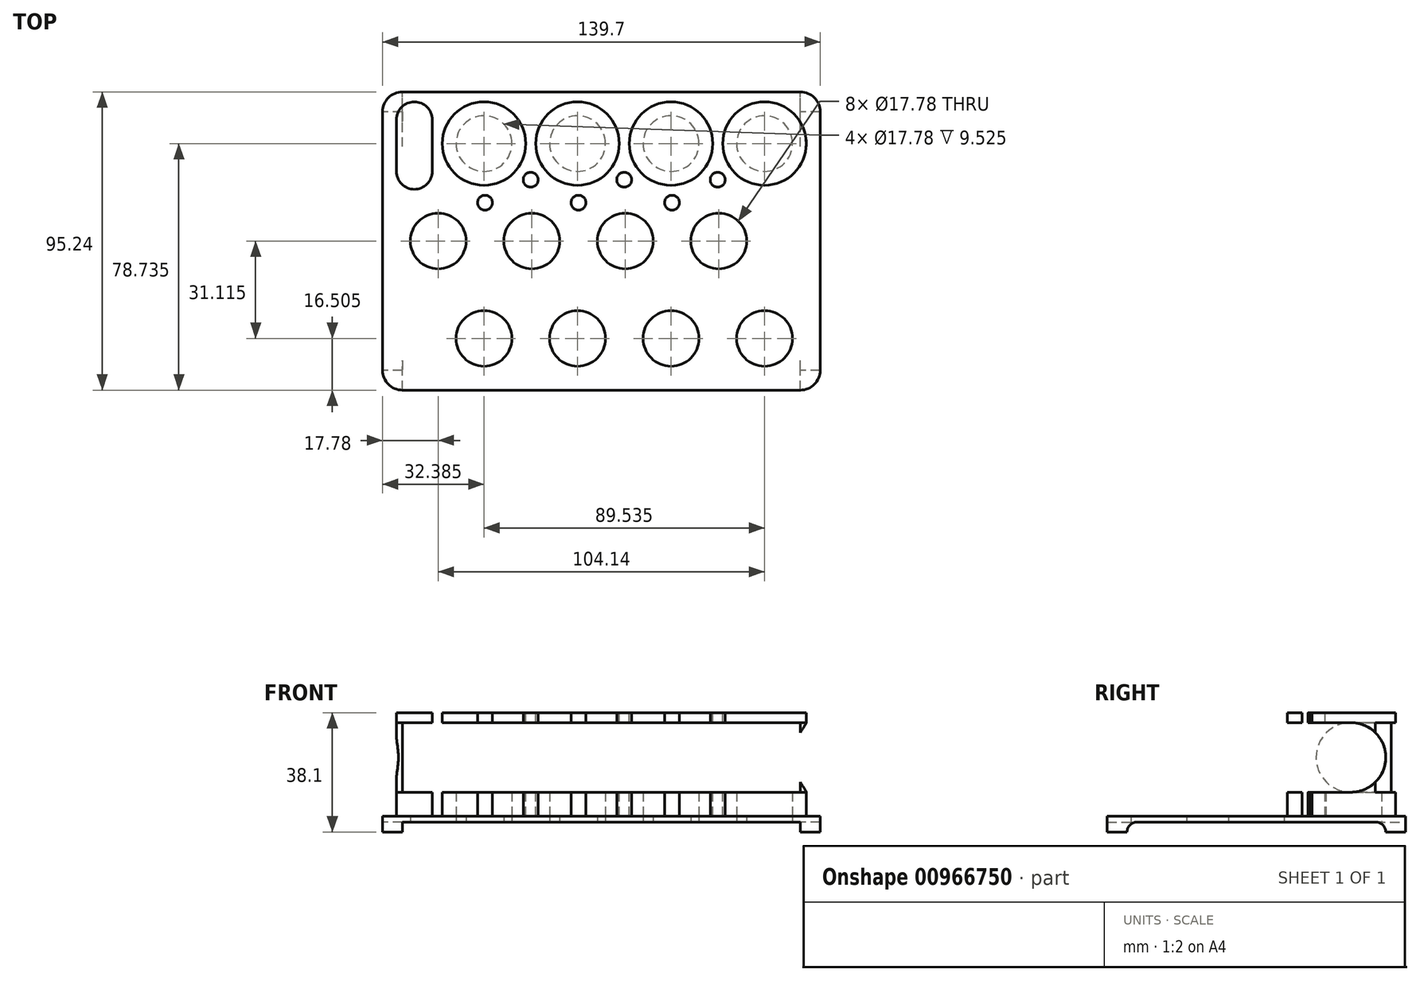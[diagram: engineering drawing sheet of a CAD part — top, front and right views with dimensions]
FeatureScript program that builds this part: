
annotation { "Feature Type Name" : "Feature", "Feature Type Description" : "" }
export const myFeature = defineFeature(function(context is Context, id is Id, definition is map)
    precondition{}
    {
        {
            var Q0;
            Q0=qCreatedBy(makeId("Right.planeOp"),FACE);
            var sketch = newSketch(context, id + "F0", { "sketchPlane" : qUnion([Q0])});
            skLineSegment(sketch, "E0.top", {"start": v(47.63, -19.05) * mm, "end": v(-47.63, -19.05) * mm});
            skLineSegment(sketch, "E0.left", {"start": v(47.63, 19.05) * mm, "end": v(47.63, -19.05) * mm});
            skLineSegment(sketch, "E0.right", {"start": v(-47.63, 19.05) * mm, "end": v(-47.63, -19.05) * mm});
            skPoint(sketch, "E0.middle", {"position": v(0, 0) * mm});
            skLineSegment(sketch, "E1.bottom", {"start": v(-41.28, -19.05) * mm, "end": v(41.27, -19.05) * mm});
            skLineSegment(sketch, "E1.top", {"start": v(-41.28, -15.88) * mm, "end": v(41.27, -15.88) * mm});
            skLineSegment(sketch, "E1.left", {"start": v(-41.28, -19.05) * mm, "end": v(-41.28, -19.05) * mm});
            skLineSegment(sketch, "E1.right", {"start": v(41.27, -19.05) * mm, "end": v(41.27, -19.05) * mm});
            skLineSegment(sketch, "E2.bottom", {"start": v(-30.16, -6.35) * mm, "end": v(30.16, -6.35) * mm});
            skLineSegment(sketch, "E2.top", {"start": v(-30.16, 15.88) * mm, "end": v(30.16, 15.88) * mm});
            skLineSegment(sketch, "E2.left", {"start": v(-41.28, 4.76) * mm, "end": v(-41.28, 4.76) * mm});
            skLineSegment(sketch, "E2.right", {"start": v(41.28, 4.76) * mm, "end": v(41.28, 4.76) * mm});
            skPoint(sketch, "E3.visualSharp", {"position": v(-41.28, -6.35) * mm});
            skPoint(sketch, "E4.visualSharp", {"position": v(41.28, -6.35) * mm});
            skPoint(sketch, "E5.visualSharp", {"position": v(-41.28, -15.88) * mm});
            skPoint(sketch, "E6.visualSharp", {"position": v(41.27, -15.88) * mm});
            skLineSegment(sketch, "E7", {"start": v(41.27, -15.88) * mm, "end": v(41.27, -15.88) * mm});
            skLineSegment(sketch, "E8", {"start": v(41.27, -15.88) * mm, "end": v(41.27, -19.05) * mm});
            skLineSegment(sketch, "E9", {"start": v(-41.28, -15.88) * mm, "end": v(-41.28, -15.88) * mm});
            skLineSegment(sketch, "E10", {"start": v(-41.28, -15.88) * mm, "end": v(-41.28, -19.05) * mm});
            skLineSegment(sketch, "E11", {"start": v(-41.28, -6.35) * mm, "end": v(-41.28, -6.35) * mm});
            skLineSegment(sketch, "E12", {"start": v(41.28, -6.35) * mm, "end": v(41.28, -6.35) * mm});
            skLineSegment(sketch, "E13", {"start": v(-47.63, 19.05) * mm, "end": v(47.63, 19.05) * mm});
            skArc(sketch, "E14.filletArc", {"start": v(-30.16, 15.88) * mm, "mid": v(-38.02, 12.62) * mm, "end": v(-41.28, 4.76) * mm});
            skArc(sketch, "E15.filletArc", {"start": v(-41.28, 4.76) * mm, "mid": v(-38.02, -3.1) * mm, "end": v(-30.16, -6.35) * mm});
            skArc(sketch, "E16.filletArc", {"start": v(41.28, 4.76) * mm, "mid": v(38.02, 12.62) * mm, "end": v(30.16, 15.88) * mm});
            skArc(sketch, "E17.filletArc", {"start": v(30.16, -6.35) * mm, "mid": v(38.02, -3.1) * mm, "end": v(41.28, 4.76) * mm});
            skSolve(sketch);
        }
        {
            var Q0;
            {var subQ0=sQuery(id+"F0.wireOp",EDGE,"E0.left");Q0=makeQuery(id+"F0.imprint","IMPRINT",FACE,{"disambiguationData":[TD([[makeQuery(id+"F0.imprint","IMPRINT",EDGE,{"derivedFrom":subQ0}),-1.0]])]});}
            extrude(context, id + "F1", {"entities" : qUnion([Q0]), "depth" : 139.7 * mm, "offsetDistance" : 25.4 * mm});
        }
        {
            var Q0;
            Q0=makeQuery(id+"F1.opExtrude","SWEPT_FACE",FACE,{"disambiguationData":[OSD([sQuery(id+"F0.wireOp",EDGE,"E0.left")])]});
            var sketch = newSketch(context, id + "F2", { "sketchPlane" : qUnion([Q0])});
            skLineSegment(sketch, "E18.bottom", {"start": v(-133.35, -19.05) * mm, "end": v(-6.35, -19.05) * mm});
            skLineSegment(sketch, "E18.top", {"start": v(-133.35, -15.88) * mm, "end": v(-6.35, -15.88) * mm});
            skLineSegment(sketch, "E18.left", {"start": v(-133.35, -19.05) * mm, "end": v(-133.35, -19.05) * mm});
            skLineSegment(sketch, "E18.right", {"start": v(-6.35, -19.05) * mm, "end": v(-6.35, -19.05) * mm});
            skPoint(sketch, "E19.visualSharp", {"position": v(-133.35, -15.88) * mm});
            skPoint(sketch, "E20.visualSharp", {"position": v(-6.35, -15.87) * mm});
            skLineSegment(sketch, "E21.bottom", {"start": v(-136.53, -19.05) * mm, "end": v(-3.17, -19.05) * mm});
            skLineSegment(sketch, "E22", {"start": v(-133.35, -19.05) * mm, "end": v(-133.35, -15.88) * mm});
            skLineSegment(sketch, "E23", {"start": v(-133.35, -15.88) * mm, "end": v(-133.35, -15.88) * mm});
            skLineSegment(sketch, "E24", {"start": v(-6.35, -15.87) * mm, "end": v(-6.35, -15.87) * mm});
            skLineSegment(sketch, "E25", {"start": v(-6.35, -15.87) * mm, "end": v(-6.35, -19.05) * mm});
            skLineSegment(sketch, "E26.bottom", {"start": v(-133.35, 15.88) * mm, "end": v(-6.35, 15.88) * mm});
            skLineSegment(sketch, "E26.top", {"start": v(-133.35, -6.35) * mm, "end": v(-6.35, -6.35) * mm});
            skLineSegment(sketch, "E26.left", {"start": v(-133.35, 15.87) * mm, "end": v(-133.35, -6.35) * mm});
            skLineSegment(sketch, "E26.right", {"start": v(-6.35, 15.88) * mm, "end": v(-6.35, -6.35) * mm});
            skSolve(sketch);
        }
        {
            var Q0;
            Q0=makeQuery(id+"F2.imprint","IMPRINT",FACE,{"disambiguationData":[TD([[makeQuery(id+"F2.imprint","IMPRINT",EDGE,{"derivedFrom":sQuery(id+"F2.wireOp",EDGE,"E26.bottom")}),-1.0]])]});
            var Q1;
            Q1=makeQuery(id+"F2.imprint","IMPRINT",FACE,{"disambiguationData":[TD([[makeQuery(id+"F2.imprint","IMPRINT",EDGE,{"derivedFrom":sQuery(id+"F2.wireOp",EDGE,"E18.top")}),-1.0]])]});
            extrude(context, id + "F3", {"entities" : qUnion([Q0, Q1]), "operationType" : NewBodyOperationType.REMOVE, "endBound" : BoundingType.THROUGH_ALL, "oppositeDirection" : true, "depth" : 25.4 * mm, "offsetDistance" : 25.4 * mm});
        }
        {
            var Q0;
            Q0=makeQuery(id+"F1.opExtrude","SWEPT_FACE",FACE,{"disambiguationData":[OSD([sQuery(id+"F0.wireOp",EDGE,"E13")])]});
            var sketch = newSketch(context, id + "F4", { "sketchPlane" : qUnion([Q0])});
            skCircle(sketch, "E27", {"center": v(121.92, -31.12) * mm, "radius": 13.34 * mm});
            skCircle(sketch, "E28", {"center": v(92.08, -31.12) * mm, "radius": 13.34 * mm});
            skCircle(sketch, "E29", {"center": v(17.78, 0) * mm, "radius": 13.34 * mm});
            skCircle(sketch, "E30", {"center": v(47.62, 0) * mm, "radius": 13.34 * mm});
            skCircle(sketch, "E31", {"center": v(77.47, 0) * mm, "radius": 13.34 * mm});
            skCircle(sketch, "E32", {"center": v(107.32, 0) * mm, "radius": 13.34 * mm});
            skCircle(sketch, "E33", {"center": v(62.23, -31.12) * mm, "radius": 13.34 * mm});
            skCircle(sketch, "E34", {"center": v(32.39, -31.12) * mm, "radius": 13.34 * mm});
            skCircle(sketch, "E35.MirrorC", {"center": v(32.39, 31.12) * mm, "radius": 13.34 * mm});
            skCircle(sketch, "E36.MirrorC", {"center": v(62.23, 31.12) * mm, "radius": 13.34 * mm});
            skCircle(sketch, "E37.MirrorC", {"center": v(92.08, 31.12) * mm, "radius": 13.34 * mm});
            skCircle(sketch, "E38.MirrorC", {"center": v(121.92, 31.12) * mm, "radius": 13.34 * mm});
            skLineSegment(sketch, "E39.bottom", {"start": v(129.54, -14.6) * mm, "end": v(129.54, -14.6) * mm});
            skLineSegment(sketch, "E39.top", {"start": v(129.54, 14.6) * mm, "end": v(129.54, 14.6) * mm});
            skLineSegment(sketch, "E39.left", {"start": v(135.26, -8.9) * mm, "end": v(135.26, 8.9) * mm});
            skLineSegment(sketch, "E39.right", {"start": v(123.83, -8.9) * mm, "end": v(123.83, 8.9) * mm});
            skPoint(sketch, "E40.visualSharp", {"position": v(135.26, -14.6) * mm});
            skArc(sketch, "E40.filletArc", {"start": v(129.54, -14.6) * mm, "mid": v(133.58, -12.93) * mm, "end": v(135.26, -8.9) * mm});
            skPoint(sketch, "E41.visualSharp", {"position": v(123.83, -14.6) * mm});
            skArc(sketch, "E41.filletArc", {"start": v(123.83, -8.9) * mm, "mid": v(125.5, -12.93) * mm, "end": v(129.54, -14.6) * mm});
            skPoint(sketch, "E42.visualSharp", {"position": v(135.26, 14.6) * mm});
            skArc(sketch, "E42.filletArc", {"start": v(135.26, 8.9) * mm, "mid": v(133.58, 12.93) * mm, "end": v(129.54, 14.6) * mm});
            skPoint(sketch, "E43.visualSharp", {"position": v(123.83, 14.6) * mm});
            skArc(sketch, "E43.filletArc", {"start": v(129.54, 14.6) * mm, "mid": v(125.5, 12.93) * mm, "end": v(123.83, 8.9) * mm});
            skPoint(sketch, "E44", {"position": v(106.98, -19.56) * mm});
            skCircle(sketch, "E45", {"center": v(106.98, -19.56) * mm, "radius": 2.38 * mm});
            skCircle(sketch, "E46", {"center": v(77.13, -19.56) * mm, "radius": 2.38 * mm});
            skCircle(sketch, "E47", {"center": v(47.29, -19.56) * mm, "radius": 2.38 * mm});
            skCircle(sketch, "E48", {"center": v(92.4, -12.23) * mm, "radius": 2.38 * mm});
            skCircle(sketch, "E49", {"center": v(62.56, -12.23) * mm, "radius": 2.38 * mm});
            skCircle(sketch, "E50", {"center": v(32.71, -12.23) * mm, "radius": 2.38 * mm});
            skCircle(sketch, "E51.MirrorC", {"center": v(106.98, 19.56) * mm, "radius": 2.38 * mm});
            skCircle(sketch, "E52.MirrorC", {"center": v(77.13, 19.56) * mm, "radius": 2.38 * mm});
            skCircle(sketch, "E53.MirrorC", {"center": v(47.29, 19.56) * mm, "radius": 2.38 * mm});
            skCircle(sketch, "E54.MirrorC", {"center": v(92.4, 12.23) * mm, "radius": 2.38 * mm});
            skCircle(sketch, "E55.MirrorC", {"center": v(62.56, 12.23) * mm, "radius": 2.38 * mm});
            skCircle(sketch, "E56.MirrorC", {"center": v(32.71, 12.23) * mm, "radius": 2.38 * mm});
            skLineSegment(sketch, "E57.bottom", {"start": v(10.16, -44.45) * mm, "end": v(10.16, -44.45) * mm});
            skLineSegment(sketch, "E57.top", {"start": v(10.16, -16.51) * mm, "end": v(10.16, -16.51) * mm});
            skLineSegment(sketch, "E57.left", {"start": v(15.88, -38.74) * mm, "end": v(15.88, -22.23) * mm});
            skLineSegment(sketch, "E57.right", {"start": v(4.45, -38.74) * mm, "end": v(4.45, -22.23) * mm});
            skPoint(sketch, "E58.visualSharp", {"position": v(15.88, -44.45) * mm});
            skArc(sketch, "E58.filletArc", {"start": v(10.16, -44.45) * mm, "mid": v(14.2, -42.78) * mm, "end": v(15.88, -38.74) * mm});
            skPoint(sketch, "E59.visualSharp", {"position": v(4.45, -44.45) * mm});
            skArc(sketch, "E59.filletArc", {"start": v(4.45, -38.74) * mm, "mid": v(6.12, -42.78) * mm, "end": v(10.16, -44.45) * mm});
            skPoint(sketch, "E60.visualSharp", {"position": v(15.88, -16.51) * mm});
            skArc(sketch, "E60.filletArc", {"start": v(15.88, -22.23) * mm, "mid": v(14.2, -18.18) * mm, "end": v(10.16, -16.51) * mm});
            skPoint(sketch, "E61.visualSharp", {"position": v(4.44, -16.51) * mm});
            skArc(sketch, "E61.filletArc", {"start": v(10.16, -16.51) * mm, "mid": v(6.12, -18.18) * mm, "end": v(4.44, -22.23) * mm});
            skPoint(sketch, "E62.MirrorP", {"position": v(15.88, 16.51) * mm});
            skPoint(sketch, "E63.MirrorP", {"position": v(15.88, 44.45) * mm});
            skArc(sketch, "E64.MirrorCS", {"start": v(15.88, 22.23) * mm, "mid": v(14.2, 18.18) * mm, "end": v(10.16, 16.51) * mm});
            skPoint(sketch, "E65.MirrorP", {"position": v(4.45, 44.45) * mm});
            skPoint(sketch, "E66.MirrorP", {"position": v(4.44, 16.51) * mm});
            skLineSegment(sketch, "E67.MirrorCS", {"start": v(10.16, 44.45) * mm, "end": v(10.16, 44.45) * mm});
            skLineSegment(sketch, "E68.MirrorCS", {"start": v(4.45, 38.74) * mm, "end": v(4.45, 22.23) * mm});
            skArc(sketch, "E69.MirrorCS", {"start": v(10.16, 16.51) * mm, "mid": v(6.12, 18.18) * mm, "end": v(4.44, 22.23) * mm});
            skArc(sketch, "E70.MirrorCS", {"start": v(10.16, 44.45) * mm, "mid": v(14.2, 42.78) * mm, "end": v(15.88, 38.74) * mm});
            skLineSegment(sketch, "E71.MirrorCS", {"start": v(15.88, 38.74) * mm, "end": v(15.88, 22.23) * mm});
            skArc(sketch, "E72.MirrorCS", {"start": v(4.45, 38.74) * mm, "mid": v(6.12, 42.78) * mm, "end": v(10.16, 44.45) * mm});
            skLineSegment(sketch, "E73.MirrorCS", {"start": v(10.16, 16.51) * mm, "end": v(10.16, 16.51) * mm});
            skSolve(sketch);
        }
        {
            var Q0;
            Q0=makeQuery(id+"F4.imprint","IMPRINT",FACE,{"disambiguationData":[TD([[makeQuery(id+"F4.imprint","IMPRINT",EDGE,{"derivedFrom":sQuery(id+"F4.wireOp",EDGE,"E27")}),1.0]])]});
            var Q1;
            Q1=makeQuery(id+"F4.imprint","IMPRINT",FACE,{"disambiguationData":[TD([[makeQuery(id+"F4.imprint","IMPRINT",EDGE,{"derivedFrom":sQuery(id+"F4.wireOp",EDGE,"E28")}),1.0]])]});
            var Q2;
            Q2=makeQuery(id+"F4.imprint","IMPRINT",FACE,{"disambiguationData":[TD([[makeQuery(id+"F4.imprint","IMPRINT",EDGE,{"derivedFrom":sQuery(id+"F4.wireOp",EDGE,"E33")}),1.0]])]});
            var Q3;
            Q3=makeQuery(id+"F4.imprint","IMPRINT",FACE,{"disambiguationData":[TD([[makeQuery(id+"F4.imprint","IMPRINT",EDGE,{"derivedFrom":sQuery(id+"F4.wireOp",EDGE,"E34")}),1.0]])]});
            var Q4;
            Q4=makeQuery(id+"F4.imprint","IMPRINT",FACE,{"disambiguationData":[TD([[makeQuery(id+"F4.imprint","IMPRINT",EDGE,{"derivedFrom":sQuery(id+"F4.wireOp",EDGE,"AhIFXKle-6ren-T3tb-L6Av-1iPCFqoMsREZ")}),1.0]])]});
            var Q5;
            Q5=makeQuery(id+"F4.imprint","IMPRINT",FACE,{"disambiguationData":[TD([[makeQuery(id+"F4.imprint","IMPRINT",EDGE,{"derivedFrom":sQuery(id+"F4.wireOp",EDGE,"wPVB1F3V-20fs-MMbR-FTxM-zm3m0jVc7lvQ")}),1.0]])]});
            var Q6;
            Q6=makeQuery(id+"F4.imprint","IMPRINT",FACE,{"disambiguationData":[TD([[makeQuery(id+"F4.imprint","IMPRINT",EDGE,{"derivedFrom":sQuery(id+"F4.wireOp",EDGE,"T3ZcG9Cn-MawP-cxRy-pQcX-JEefpN5sOvam")}),1.0]])]});
            var Q7;
            Q7=makeQuery(id+"F4.imprint","IMPRINT",FACE,{"disambiguationData":[TD([[makeQuery(id+"F4.imprint","IMPRINT",EDGE,{"derivedFrom":sQuery(id+"F4.wireOp",EDGE,"XZ3QAXgJ-CkEy-Kyhc-Jaey-V5kokyXw6pyG")}),1.0]])]});
            var Q8;
            Q8=makeQuery(id+"F4.imprint","IMPRINT",FACE,{"disambiguationData":[TD([[makeQuery(id+"F4.imprint","IMPRINT",EDGE,{"derivedFrom":sQuery(id+"F4.wireOp",EDGE,"E29")}),1.0]])]});
            var Q9;
            Q9=makeQuery(id+"F4.imprint","IMPRINT",FACE,{"disambiguationData":[TD([[makeQuery(id+"F4.imprint","IMPRINT",EDGE,{"derivedFrom":sQuery(id+"F4.wireOp",EDGE,"E30")}),1.0]])]});
            var Q10;
            Q10=makeQuery(id+"F4.imprint","IMPRINT",FACE,{"disambiguationData":[TD([[makeQuery(id+"F4.imprint","IMPRINT",EDGE,{"derivedFrom":sQuery(id+"F4.wireOp",EDGE,"E31")}),1.0]])]});
            var Q11;
            Q11=makeQuery(id+"F4.imprint","IMPRINT",FACE,{"disambiguationData":[TD([[makeQuery(id+"F4.imprint","IMPRINT",EDGE,{"derivedFrom":sQuery(id+"F4.wireOp",EDGE,"E32")}),1.0]])]});
            var Q12;
            Q12=makeQuery(id+"F4.imprint","IMPRINT",FACE,{"disambiguationData":[TD([[makeQuery(id+"F4.imprint","IMPRINT",EDGE,{"derivedFrom":sQuery(id+"F4.wireOp",EDGE,"E39.bottom")}),-1.0]])]});
            var Q13;
            Q13=makeQuery(id+"F4.imprint","IMPRINT",FACE,{"disambiguationData":[TD([[makeQuery(id+"F4.imprint","IMPRINT",EDGE,{"derivedFrom":sQuery(id+"F4.wireOp",EDGE,"E38.MirrorC")}),-1.0]])]});
            var Q14;
            Q14=makeQuery(id+"F4.imprint","IMPRINT",FACE,{"disambiguationData":[TD([[makeQuery(id+"F4.imprint","IMPRINT",EDGE,{"derivedFrom":sQuery(id+"F4.wireOp",EDGE,"E37.MirrorC")}),-1.0]])]});
            var Q15;
            Q15=makeQuery(id+"F4.imprint","IMPRINT",FACE,{"disambiguationData":[TD([[makeQuery(id+"F4.imprint","IMPRINT",EDGE,{"derivedFrom":sQuery(id+"F4.wireOp",EDGE,"E36.MirrorC")}),-1.0]])]});
            var Q16;
            Q16=makeQuery(id+"F4.imprint","IMPRINT",FACE,{"disambiguationData":[TD([[makeQuery(id+"F4.imprint","IMPRINT",EDGE,{"derivedFrom":sQuery(id+"F4.wireOp",EDGE,"E35.MirrorC")}),-1.0]])]});
            var Q17;
            Q17=makeQuery(id+"F4.imprint","IMPRINT",FACE,{"disambiguationData":[TD([[makeQuery(id+"F4.imprint","IMPRINT",EDGE,{"derivedFrom":sQuery(id+"F4.wireOp",EDGE,"c6291b78-575e-4a72-a550-4777f93526100.MirrorC")}),-1.0]])]});
            var Q18;
            Q18=makeQuery(id+"F4.imprint","IMPRINT",FACE,{"disambiguationData":[TD([[makeQuery(id+"F4.imprint","IMPRINT",EDGE,{"derivedFrom":sQuery(id+"F4.wireOp",EDGE,"f3e2f5e7-102e-45df-8559-8a6ab0aaba5b0.MirrorC")}),-1.0]])]});
            var Q19;
            Q19=makeQuery(id+"F4.imprint","IMPRINT",FACE,{"disambiguationData":[TD([[makeQuery(id+"F4.imprint","IMPRINT",EDGE,{"derivedFrom":sQuery(id+"F4.wireOp",EDGE,"dd626ad0-a420-4f17-bbb8-cdf8eb234abf0.MirrorC")}),-1.0]])]});
            var Q20;
            Q20=makeQuery(id+"F4.imprint","IMPRINT",FACE,{"disambiguationData":[TD([[makeQuery(id+"F4.imprint","IMPRINT",EDGE,{"derivedFrom":sQuery(id+"F4.wireOp",EDGE,"f3a2bc9c-32a0-4c81-a079-4487179850330.MirrorC")}),-1.0]])]});
            var Q21;
            Q21=makeQuery(id+"F4.imprint","IMPRINT",FACE,{"disambiguationData":[TD([[makeQuery(id+"F4.imprint","IMPRINT",EDGE,{"derivedFrom":sQuery(id+"F4.wireOp",EDGE,"E57.bottom")}),-1.0]])]});
            var Q22;
            Q22=makeQuery(id+"F4.imprint","IMPRINT",FACE,{"disambiguationData":[TD([[makeQuery(id+"F4.imprint","IMPRINT",EDGE,{"derivedFrom":sQuery(id+"F4.wireOp",EDGE,"E64.MirrorCS")}),-1.0]])]});
            var Q23;
            Q23=makeQuery(id+"F4.imprint","IMPRINT",FACE,{"disambiguationData":[TD([[makeQuery(id+"F4.imprint","IMPRINT",EDGE,{"derivedFrom":sQuery(id+"F4.wireOp",EDGE,"E51.MirrorC")}),-1.0]])]});
            var Q24;
            Q24=makeQuery(id+"F4.imprint","IMPRINT",FACE,{"disambiguationData":[TD([[makeQuery(id+"F4.imprint","IMPRINT",EDGE,{"derivedFrom":sQuery(id+"F4.wireOp",EDGE,"E54.MirrorC")}),-1.0]])]});
            var Q25;
            Q25=makeQuery(id+"F4.imprint","IMPRINT",FACE,{"disambiguationData":[TD([[makeQuery(id+"F4.imprint","IMPRINT",EDGE,{"derivedFrom":sQuery(id+"F4.wireOp",EDGE,"E52.MirrorC")}),-1.0]])]});
            var Q26;
            Q26=makeQuery(id+"F4.imprint","IMPRINT",FACE,{"disambiguationData":[TD([[makeQuery(id+"F4.imprint","IMPRINT",EDGE,{"derivedFrom":sQuery(id+"F4.wireOp",EDGE,"E55.MirrorC")}),-1.0]])]});
            var Q27;
            Q27=makeQuery(id+"F4.imprint","IMPRINT",FACE,{"disambiguationData":[TD([[makeQuery(id+"F4.imprint","IMPRINT",EDGE,{"derivedFrom":sQuery(id+"F4.wireOp",EDGE,"E53.MirrorC")}),-1.0]])]});
            var Q28;
            Q28=makeQuery(id+"F4.imprint","IMPRINT",FACE,{"disambiguationData":[TD([[makeQuery(id+"F4.imprint","IMPRINT",EDGE,{"derivedFrom":sQuery(id+"F4.wireOp",EDGE,"E56.MirrorC")}),-1.0]])]});
            var Q29;
            Q29=makeQuery(id+"F4.imprint","IMPRINT",FACE,{"disambiguationData":[TD([[makeQuery(id+"F4.imprint","IMPRINT",EDGE,{"derivedFrom":sQuery(id+"F4.wireOp",EDGE,"E50")}),1.0]])]});
            var Q30;
            Q30=makeQuery(id+"F4.imprint","IMPRINT",FACE,{"disambiguationData":[TD([[makeQuery(id+"F4.imprint","IMPRINT",EDGE,{"derivedFrom":sQuery(id+"F4.wireOp",EDGE,"E47")}),1.0]])]});
            var Q31;
            Q31=makeQuery(id+"F4.imprint","IMPRINT",FACE,{"disambiguationData":[TD([[makeQuery(id+"F4.imprint","IMPRINT",EDGE,{"derivedFrom":sQuery(id+"F4.wireOp",EDGE,"E49")}),1.0]])]});
            var Q32;
            Q32=makeQuery(id+"F4.imprint","IMPRINT",FACE,{"disambiguationData":[TD([[makeQuery(id+"F4.imprint","IMPRINT",EDGE,{"derivedFrom":sQuery(id+"F4.wireOp",EDGE,"E46")}),1.0]])]});
            var Q33;
            Q33=makeQuery(id+"F4.imprint","IMPRINT",FACE,{"disambiguationData":[TD([[makeQuery(id+"F4.imprint","IMPRINT",EDGE,{"derivedFrom":sQuery(id+"F4.wireOp",EDGE,"E48")}),1.0]])]});
            var Q34;
            Q34=makeQuery(id+"F4.imprint","IMPRINT",FACE,{"disambiguationData":[TD([[makeQuery(id+"F4.imprint","IMPRINT",EDGE,{"derivedFrom":sQuery(id+"F4.wireOp",EDGE,"E45")}),1.0]])]});
            var Q35;
            Q35=makeQuery(id+"F4.imprint","IMPRINT",FACE,{"disambiguationData":[TD([[makeQuery(id+"F4.imprint","IMPRINT",EDGE,{"derivedFrom":sQuery(id+"F4.wireOp",EDGE,"E57.left")}),1.0]])]});
            var Q36;
            Q36=makeQuery(id+"F4.imprint","IMPRINT",FACE,{"disambiguationData":[TD([[makeQuery(id+"F4.imprint","IMPRINT",EDGE,{"derivedFrom":sQuery(id+"F4.wireOp",EDGE,"E39.left")}),1.0]])]});
            extrude(context, id + "F5", {"entities" : qUnion([Q0, Q1, Q2, Q3, Q4, Q5, Q6, Q7, Q8, Q9, Q10, Q11, Q12, Q13, Q14, Q15, Q16, Q17, Q18, Q19, Q20, Q21, Q22, Q23, Q24, Q25, Q26, Q27, Q28, Q29, Q30, Q31, Q32, Q33, Q34, Q35, Q36]), "operationType" : NewBodyOperationType.REMOVE, "oppositeDirection" : true, "depth" : 33.02 * mm, "offsetDistance" : 25.4 * mm});
        }
        {
            var Q0;
            Q0=makeQuery(id+"F1.opExtrude","CAP_EDGE",EDGE,{"disambiguationData":[OSD([sQuery(id+"F0.wireOp",EDGE,"E0.left")])],"isStart":true});
            var Q1;
            Q1=makeQuery(id+"F1.opExtrude","CAP_EDGE",EDGE,{"disambiguationData":[OSD([sQuery(id+"F0.wireOp",EDGE,"E0.right")])],"isStart":true});
            var Q2;
            Q2=makeQuery(id+"F1.opExtrude","CAP_EDGE",EDGE,{"disambiguationData":[OSD([sQuery(id+"F0.wireOp",EDGE,"E0.right")])],"isStart":false});
            var Q3;
            Q3=makeQuery(id+"F1.opExtrude","CAP_EDGE",EDGE,{"disambiguationData":[OSD([sQuery(id+"F0.wireOp",EDGE,"E0.left")])],"isStart":false});
            fillet(context, id + "F6", {"entities" : qUnion([Q0, Q1, Q2, Q3]), "radius" : 6.35 * mm, "tangentPropagation" : true, "allowEdgeOverflow" : false});
        }
        {
            var Q0;
            Q0=makeQuery(id+"F3.boolean.opBoolean","MERGE",FACE,{"derivedFrom":[makeQuery(id+"F1.opExtrude","SWEPT_FACE",FACE,{"disambiguationData":[OSD([sQuery(id+"F0.wireOp",EDGE,"E1.top")])]})],"fromTools":[makeQuery(id+"F3.opExtrude","SWEPT_FACE",FACE,{"disambiguationData":[OSD([sQuery(id+"F2.wireOp",EDGE,"E18.top")])]})]});
            var sketch = newSketch(context, id + "F7", { "sketchPlane" : qUnion([Q0])});
            skCircle(sketch, "E74", {"center": v(17.78, 0) * mm, "radius": 8.9 * mm});
            skCircle(sketch, "E75", {"center": v(47.62, 0) * mm, "radius": 8.9 * mm});
            skCircle(sketch, "E76", {"center": v(77.47, 0) * mm, "radius": 8.9 * mm});
            skCircle(sketch, "E77", {"center": v(107.32, 0) * mm, "radius": 8.9 * mm});
            skCircle(sketch, "E78", {"center": v(121.92, -31.12) * mm, "radius": 8.9 * mm});
            skCircle(sketch, "E79", {"center": v(92.08, -31.12) * mm, "radius": 8.9 * mm});
            skCircle(sketch, "E80", {"center": v(62.23, -31.12) * mm, "radius": 8.9 * mm});
            skCircle(sketch, "E81", {"center": v(32.39, -31.12) * mm, "radius": 8.9 * mm});
            skCircle(sketch, "E82.MirrorC", {"center": v(32.39, 31.12) * mm, "radius": 8.9 * mm});
            skCircle(sketch, "E83.MirrorC", {"center": v(62.23, 31.12) * mm, "radius": 8.9 * mm});
            skCircle(sketch, "E84.MirrorC", {"center": v(92.08, 31.12) * mm, "radius": 8.9 * mm});
            skCircle(sketch, "E85.MirrorC", {"center": v(121.92, 31.12) * mm, "radius": 8.9 * mm});
            skSolve(sketch);
        }
        {
            var Q0;
            Q0 = qSketchRegion(id + "F7", true);
            extrude(context, id + "F8", {"entities" : qUnion([Q0]), "operationType" : NewBodyOperationType.REMOVE, "endBound" : BoundingType.SYMMETRIC, "oppositeDirection" : true, "depth" : 25.4 * mm, "offsetDistance" : 25.4 * mm});
        }
        {
            var Q0;
            {var subQ0=sQuery(id+"F0.wireOp",EDGE,"E10");var subQ1=sQuery(id+"F0.wireOp",EDGE,"E1.top");Q0=makeQuery(id+"F3.boolean.opBoolean","SPLIT",EDGE,{"disambiguationData":[TD([makeQuery(id+"F3.opExtrude","SWEPT_FACE",FACE,{"disambiguationData":[OSD([sQuery(id+"F2.wireOp",EDGE,"E22")])]})])],"derivedFrom":makeQuery(id+"F1.opExtrude","SWEPT_EDGE",EDGE,{"disambiguationData":[OSD([subQ1,subQ0])]})});}
            var Q1;
            {var subQ0=sQuery(id+"F0.wireOp",EDGE,"E8");var subQ1=sQuery(id+"F0.wireOp",EDGE,"E1.top");Q1=makeQuery(id+"F3.boolean.opBoolean","SPLIT",EDGE,{"disambiguationData":[TD([makeQuery(id+"F3.opExtrude","SWEPT_FACE",FACE,{"disambiguationData":[OSD([sQuery(id+"F2.wireOp",EDGE,"E22")])]})])],"derivedFrom":makeQuery(id+"F1.opExtrude","SWEPT_EDGE",EDGE,{"disambiguationData":[OSD([subQ1,subQ0])]})});}
            var Q2;
            {var subQ0=sQuery(id+"F0.wireOp",EDGE,"E8");var subQ1=sQuery(id+"F0.wireOp",EDGE,"E1.top");Q2=makeQuery(id+"F3.boolean.opBoolean","SPLIT",EDGE,{"disambiguationData":[TD([makeQuery(id+"F3.opExtrude","SWEPT_FACE",FACE,{"disambiguationData":[OSD([sQuery(id+"F2.wireOp",EDGE,"E25")])]})])],"derivedFrom":makeQuery(id+"F1.opExtrude","SWEPT_EDGE",EDGE,{"disambiguationData":[OSD([subQ1,subQ0])]})});}
            var Q3;
            {var subQ0=sQuery(id+"F0.wireOp",EDGE,"E10");var subQ1=sQuery(id+"F0.wireOp",EDGE,"E1.top");Q3=makeQuery(id+"F3.boolean.opBoolean","SPLIT",EDGE,{"disambiguationData":[TD([makeQuery(id+"F3.opExtrude","SWEPT_FACE",FACE,{"disambiguationData":[OSD([sQuery(id+"F2.wireOp",EDGE,"E25")])]})])],"derivedFrom":makeQuery(id+"F1.opExtrude","SWEPT_EDGE",EDGE,{"disambiguationData":[OSD([subQ1,subQ0])]})});}
            fillet(context, id + "F9", {"entities" : qUnion([Q0, Q1, Q2, Q3]), "radius" : 3.17 * mm, "tangentPropagation" : true, "allowEdgeOverflow" : false});
        }
    });
